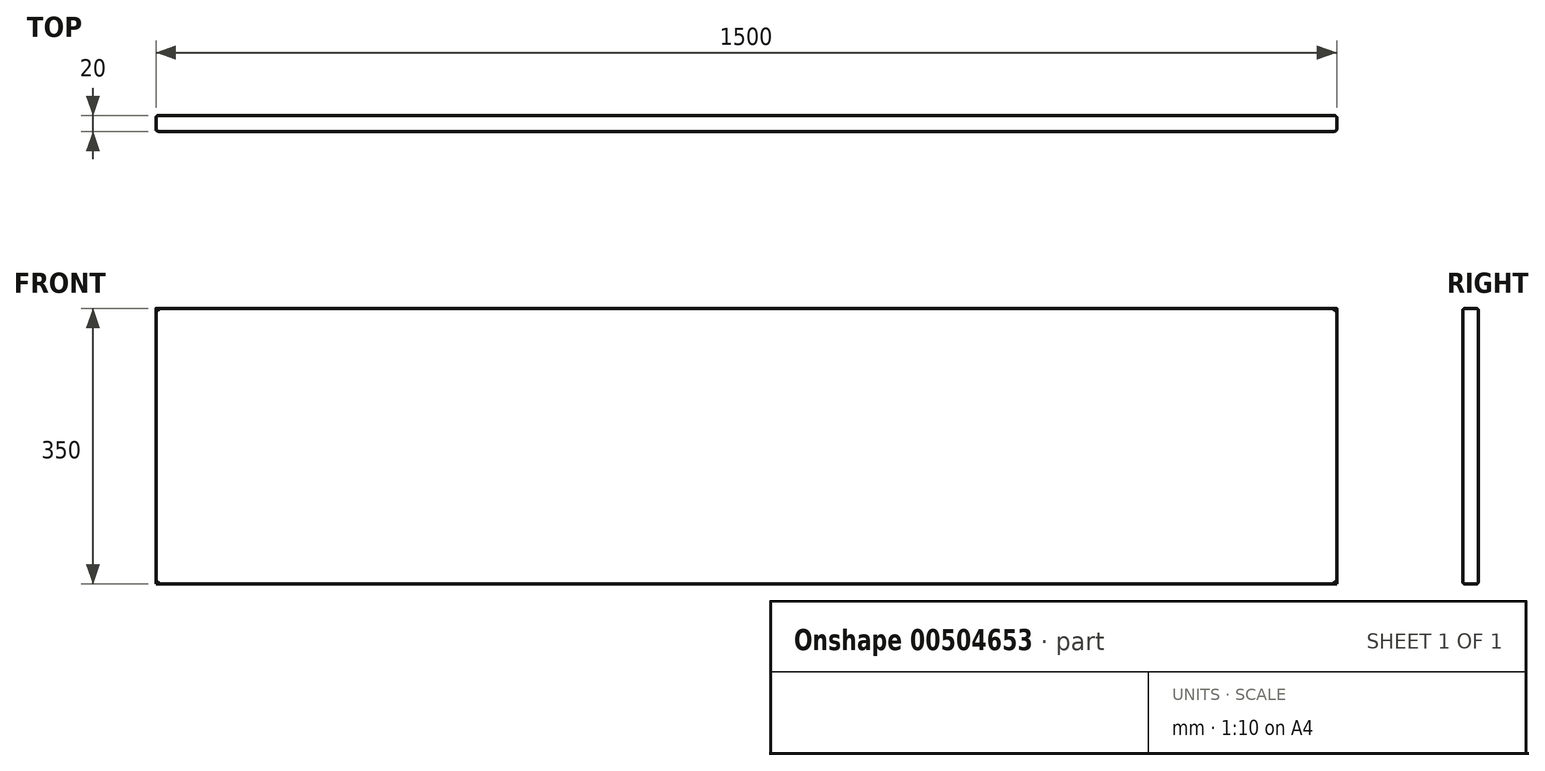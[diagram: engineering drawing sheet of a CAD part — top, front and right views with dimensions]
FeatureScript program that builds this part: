
annotation { "Feature Type Name" : "Feature", "Feature Type Description" : "" }
export const myFeature = defineFeature(function(context is Context, id is Id, definition is map)
    precondition{}
    {
        {
            var Q0;
            Q0=qCreatedBy(makeId("Front.planeOp"),FACE);
            var sketch = newSketch(context, id + "F0", { "sketchPlane" : qUnion([Q0])});
            skLineSegment(sketch, "E0.bottom", {"start": v(-278.97, 187.3) * mm, "end": v(1221.03, 187.3) * mm});
            skLineSegment(sketch, "E0.top", {"start": v(-278.97, -162.7) * mm, "end": v(1221.03, -162.7) * mm});
            skLineSegment(sketch, "E0.left", {"start": v(-278.97, 187.3) * mm, "end": v(-278.97, -162.7) * mm});
            skLineSegment(sketch, "E0.right", {"start": v(1221.03, 187.3) * mm, "end": v(1221.03, -162.7) * mm});
            skSolve(sketch);
        }
        {
            var Q0;
            Q0 = qSketchRegion(id + "F0", true);
            extrude(context, id + "F1", {"entities" : qUnion([Q0]), "depth" : 20 * mm});
        }
        {
            var Q0;
            Q0=makeQuery(id+"F1.opExtrude","CAP_FACE",FACE,{"disambiguationData":[OSD([sQuery(id+"F0.wireOp",EDGE,"E0.bottom"),sQuery(id+"F0.wireOp",EDGE,"E0.top"),sQuery(id+"F0.wireOp",EDGE,"E0.left"),sQuery(id+"F0.wireOp",EDGE,"E0.right")])],"isStart":false});
            var Q1;
            Q1=makeQuery(id+"F1.opExtrude","CAP_FACE",FACE,{"disambiguationData":[OSD([sQuery(id+"F0.wireOp",EDGE,"E0.bottom"),sQuery(id+"F0.wireOp",EDGE,"E0.top"),sQuery(id+"F0.wireOp",EDGE,"E0.left"),sQuery(id+"F0.wireOp",EDGE,"E0.right")])],"isStart":true});
            fillet(context, id + "F2", {"entities" : qUnion([Q0, Q1]), "radius" : 3 * mm, "tangentPropagation" : true, "allowEdgeOverflow" : false});
        }
    });
